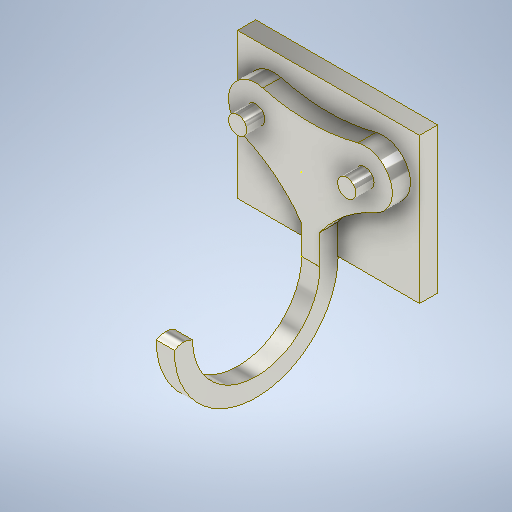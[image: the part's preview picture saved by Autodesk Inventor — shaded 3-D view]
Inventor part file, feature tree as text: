
AUTODESK INVENTOR PART (.ipt)
format: ipt  version: 2025.2 (Build 292293000, 293)  size: 329,216 bytes
history: native  units: in
note: dims shown in document units (in); Inventor stores cm internally (conversion verified against a paired STEP export)
features: sketch x15, extrude x7
ambient origin geometry x8: Origin, YZ Plane, XZ Plane, XY Plane, X Axis, Y Axis, Z Axis, Center Point
bodies: Solid1 (feature_tree)
feature tree (22):
  extrude  "Extrusion1"  Depth=0.6299in
  extrude  "Extrusion2"  Depth=0.6299in
  extrude  "Extrusion3"  Depth=1.0835in
  sketch  "Sketch4"  dims[d16=0.0394in d18=0.5906in]
  sketch  "Sketch5"  dims[d19=0.0787in d20=0.0in d21=0.0787in]
  sketch  "Sketch6"  dims[d22=0.1969in d24=0.0787in d25=0.0in]
  sketch  "Sketch7"  dims[d28=0.1969in d29=0.0in d31=0.1969in d32=0.0in]
  sketch  "Sketch8"  dims[d37=0.0787in d38=0.0in]
  extrude  "Extrusion4"  Depth=0.5906in
  sketch  "Sketch10"  dims[d44=0.0787in]
  extrude  "Extrusion5"  Depth=0.0787in
  sketch  "Sketch12"
  sketch  "Sketch13"
  extrude  "Extrusion6"  Depth=0.0787in TaperAngle=0.0deg
  extrude  "Extrusion7"  Depth=0.1969in TaperAngle=0.0deg
  sketch  "Sketch1"  dims[d0=0.7874in d1=0.6299in]
  sketch  "Sketch2"  dims[d2=0.0787in d3=0.0in d8=0.6299in]
  sketch  "Sketch3"  dims[d14=0.6111in d15=1.0835in]
  sketch  "Sketch9"  dims[d42=0.0787in d43=0.0in]
  sketch  "Sketch11"
  sketch  "Sketch14"
  sketch  "Sketch15"
